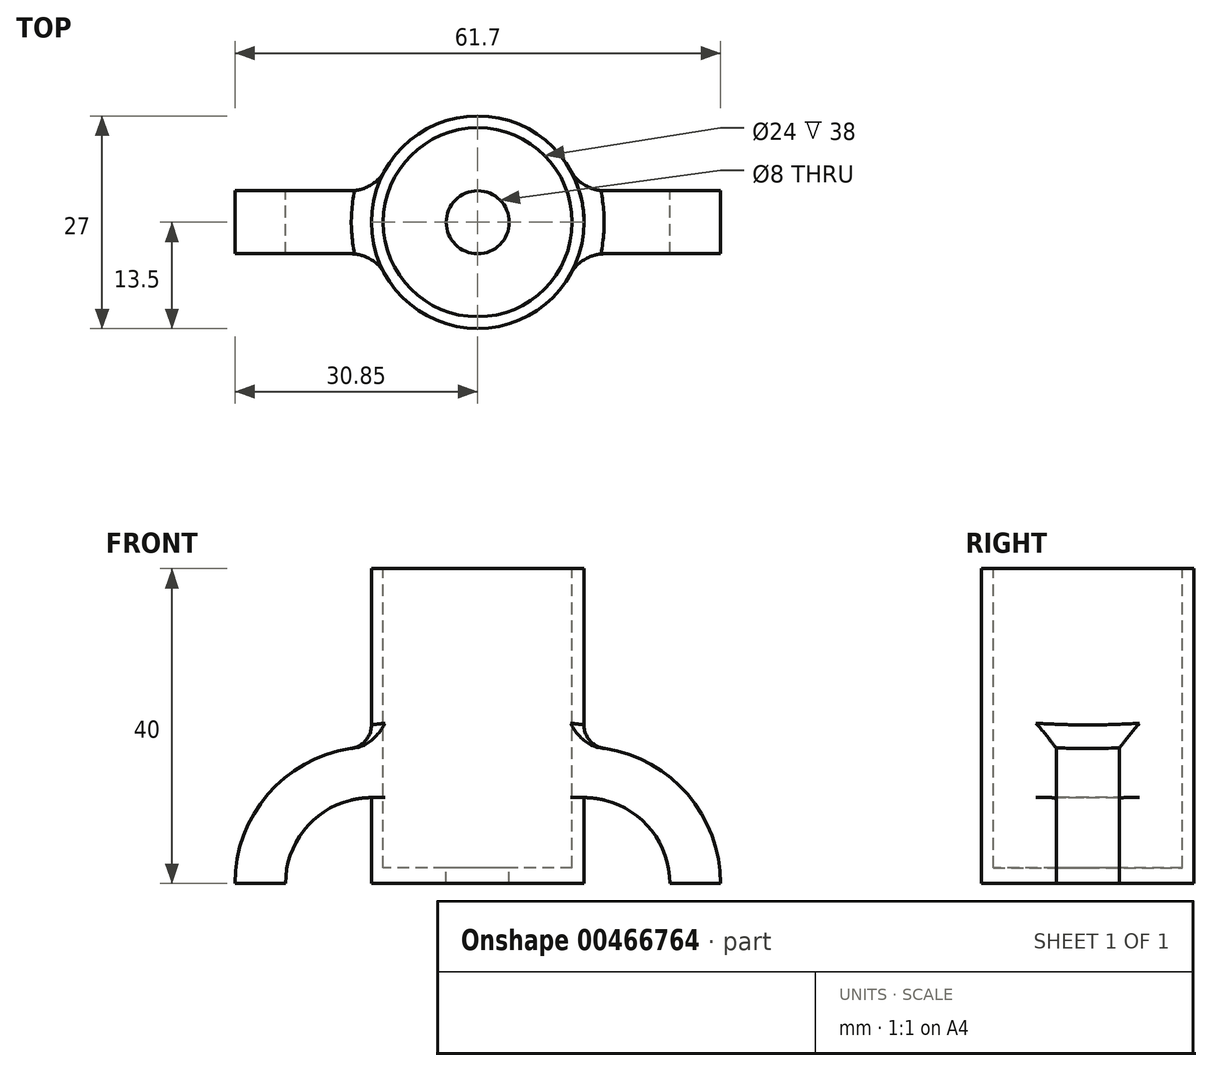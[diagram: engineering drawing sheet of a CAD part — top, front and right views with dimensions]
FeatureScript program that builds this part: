
annotation { "Feature Type Name" : "Feature", "Feature Type Description" : "" }
export const myFeature = defineFeature(function(context is Context, id is Id, definition is map)
    precondition{}
    {
        {
            var Q0;
            Q0=qCreatedBy(makeId("Top.planeOp"),FACE);
            var sketch = newSketch(context, id + "F0", { "sketchPlane" : qUnion([Q0])});
            skCircle(sketch, "E0", {"center": v(0, 0) * mm, "radius": 13.5 * mm});
            skSolve(sketch);
        }
        {
            var Q0;
            Q0=makeQuery(id+"F0.imprint","IMPRINT",FACE,{"disambiguationData":[TD([[makeQuery(id+"F0.imprint","IMPRINT",EDGE,{"derivedFrom":sQuery(id+"F0.wireOp",EDGE,"E0")}),1.0]])]});
            extrude(context, id + "F1", {"entities" : qUnion([Q0]), "depth" : 40 * mm});
        }
        {
            var Q0;
            Q0=qCreatedBy(makeId("Front.planeOp"),FACE);
            var sketch = newSketch(context, id + "F2", { "sketchPlane" : qUnion([Q0])});
            skLineSegment(sketch, "E1", {"start": v(-13.5, 0) * mm, "end": v(-13.5, 40) * mm, "construction": true});
            skLineSegment(sketch, "E2", {"start": v(13.5, 40) * mm, "end": v(13.5, 0) * mm, "construction": true});
            skArc(sketch, "E3", {"start": v(-13.5, 17.35) * mm, "mid": v(-25.77, 12.27) * mm, "end": v(-30.85, 0) * mm});
            skArc(sketch, "E4", {"start": v(-13.5, 10.91) * mm, "mid": v(-21.22, 7.72) * mm, "end": v(-24.41, 0) * mm});
            skLineSegment(sketch, "E5", {"start": v(-30.85, 0) * mm, "end": v(-24.41, 0) * mm});
            skLineSegment(sketch, "E6.bottom", {"start": v(-13.5, 17.35) * mm, "end": v(0, 17.35) * mm});
            skLineSegment(sketch, "E6.top", {"start": v(-13.5, 10.91) * mm, "end": v(0, 10.91) * mm});
            skLineSegment(sketch, "E6.left", {"start": v(-13.5, 17.35) * mm, "end": v(-13.5, 10.91) * mm});
            skLineSegment(sketch, "E6.right", {"start": v(0, 17.35) * mm, "end": v(0, 10.91) * mm});
            skArc(sketch, "E7.MirrorCS", {"start": v(13.5, 17.35) * mm, "mid": v(25.77, 12.27) * mm, "end": v(30.85, 0) * mm});
            skLineSegment(sketch, "E8.MirrorCS", {"start": v(13.5, 17.35) * mm, "end": v(0, 17.35) * mm});
            skLineSegment(sketch, "E9.MirrorCS", {"start": v(13.5, 10.91) * mm, "end": v(0, 10.91) * mm});
            skArc(sketch, "E10.MirrorCS", {"start": v(13.5, 10.91) * mm, "mid": v(21.22, 7.72) * mm, "end": v(24.41, 0) * mm});
            skLineSegment(sketch, "E11.MirrorCS", {"start": v(30.85, 0) * mm, "end": v(24.41, 0) * mm});
            skSolve(sketch);
        }
        {
            var Q0;
            Q0 = qSketchRegion(id + "F2", true);
            extrude(context, id + "F3", {"entities" : qUnion([Q0]), "operationType" : NewBodyOperationType.ADD, "endBound" : BoundingType.SYMMETRIC, "depth" : 8 * mm});
        }
        {
            var Q0;
            Q0=makeQuery(id+"F1.opExtrude","CAP_FACE",FACE,{"disambiguationData":[OSD([sQuery(id+"F0.wireOp",EDGE,"E0")])],"isStart":false});
            var sketch = newSketch(context, id + "F4", { "sketchPlane" : qUnion([Q0])});
            skCircle(sketch, "E12", {"center": v(0, 0) * mm, "radius": 12 * mm});
            skSolve(sketch);
        }
        {
            var Q0;
            Q0=makeQuery(id+"F4.imprint","IMPRINT",FACE,{"disambiguationData":[TD([[makeQuery(id+"F4.imprint","IMPRINT",EDGE,{"derivedFrom":sQuery(id+"F4.wireOp",EDGE,"E12")}),1.0]])]});
            extrude(context, id + "F5", {"entities" : qUnion([Q0]), "operationType" : NewBodyOperationType.REMOVE, "oppositeDirection" : true, "depth" : 38 * mm});
        }
        {
            var Q0;
            Q0=makeQuery(id+"F5.boolean.opBoolean","COPY",FACE,{"derivedFrom":makeQuery(id+"F5.opExtrude","CAP_FACE",FACE,{"disambiguationData":[OSD([sQuery(id+"F4.wireOp",EDGE,"E12")])],"isStart":false})});
            var sketch = newSketch(context, id + "F6", { "sketchPlane" : qUnion([Q0])});
            skCircle(sketch, "E13", {"center": v(0, 0) * mm, "radius": 4 * mm});
            skSolve(sketch);
        }
        {
            var Q0;
            Q0=makeQuery(id+"F6.imprint","IMPRINT",FACE,{"disambiguationData":[TD([[makeQuery(id+"F6.imprint","IMPRINT",EDGE,{"derivedFrom":sQuery(id+"F6.wireOp",EDGE,"E13")}),1.0]])]});
            extrude(context, id + "F7", {"entities" : qUnion([Q0]), "operationType" : NewBodyOperationType.REMOVE, "endBound" : BoundingType.UP_TO_NEXT, "oppositeDirection" : true, "depth" : 25 * mm});
        }
        {
            var Q0;
            Q0=makeQuery(id+"F3.boolean.opBoolean","INTERSECT",EDGE,{"disambiguationData":[OD(3.0)],"derivedFrom":[makeQuery(id+"F1.opExtrude","SWEPT_FACE",FACE,{"disambiguationData":[OSD([sQuery(id+"F0.wireOp",EDGE,"E0")])]}),makeQuery(id+"F3.opExtrude","SWEPT_FACE",FACE,{"disambiguationData":[OSD([sQuery(id+"F2.wireOp",EDGE,"E6.bottom"),sQuery(id+"F2.wireOp",EDGE,"E8.MirrorCS")])]})]});
            var Q1;
            Q1=makeQuery(id+"F3.boolean.opBoolean","INTERSECT",EDGE,{"disambiguationData":[OD(1.0)],"derivedFrom":[makeQuery(id+"F1.opExtrude","SWEPT_FACE",FACE,{"disambiguationData":[OSD([sQuery(id+"F0.wireOp",EDGE,"E0")])]}),makeQuery(id+"F3.opExtrude","SWEPT_FACE",FACE,{"disambiguationData":[OSD([sQuery(id+"F2.wireOp",EDGE,"E6.bottom"),sQuery(id+"F2.wireOp",EDGE,"E8.MirrorCS")])]})]});
            fillet(context, id + "F8", {"entities" : qUnion([Q0, Q1]), "radius" : 3 * mm, "tangentPropagation" : true, "allowEdgeOverflow" : false});
        }
        {
            var Q0;
            Q0=makeQuery(id+"F3.boolean.opBoolean","INTERSECT",EDGE,{"disambiguationData":[OD(1.0)],"derivedFrom":[makeQuery(id+"F1.opExtrude","SWEPT_FACE",FACE,{"disambiguationData":[OSD([sQuery(id+"F0.wireOp",EDGE,"E0")])]}),makeQuery(id+"F3.opExtrude","CAP_FACE",FACE,{"disambiguationData":[OSD([sQuery(id+"F2.wireOp",EDGE,"E3"),sQuery(id+"F2.wireOp",EDGE,"E4"),sQuery(id+"F2.wireOp",EDGE,"E5"),sQuery(id+"F2.wireOp",EDGE,"E6.bottom"),sQuery(id+"F2.wireOp",EDGE,"E6.top"),sQuery(id+"F2.wireOp",EDGE,"E7.MirrorCS"),sQuery(id+"F2.wireOp",EDGE,"E8.MirrorCS"),sQuery(id+"F2.wireOp",EDGE,"E9.MirrorCS"),sQuery(id+"F2.wireOp",EDGE,"E10.MirrorCS"),sQuery(id+"F2.wireOp",EDGE,"E11.MirrorCS")])],"isStart":true})]});
            var Q1;
            Q1=makeQuery(id+"F3.boolean.opBoolean","INTERSECT",EDGE,{"disambiguationData":[OD(1.0)],"derivedFrom":[makeQuery(id+"F1.opExtrude","SWEPT_FACE",FACE,{"disambiguationData":[OSD([sQuery(id+"F0.wireOp",EDGE,"E0")])]}),makeQuery(id+"F3.opExtrude","CAP_FACE",FACE,{"disambiguationData":[OSD([sQuery(id+"F2.wireOp",EDGE,"E3"),sQuery(id+"F2.wireOp",EDGE,"E4"),sQuery(id+"F2.wireOp",EDGE,"E5"),sQuery(id+"F2.wireOp",EDGE,"E6.bottom"),sQuery(id+"F2.wireOp",EDGE,"E6.top"),sQuery(id+"F2.wireOp",EDGE,"E7.MirrorCS"),sQuery(id+"F2.wireOp",EDGE,"E8.MirrorCS"),sQuery(id+"F2.wireOp",EDGE,"E9.MirrorCS"),sQuery(id+"F2.wireOp",EDGE,"E10.MirrorCS"),sQuery(id+"F2.wireOp",EDGE,"E11.MirrorCS")])],"isStart":false})]});
            var Q2;
            Q2=makeQuery(id+"F3.boolean.opBoolean","INTERSECT",EDGE,{"disambiguationData":[OD(0.0)],"derivedFrom":[makeQuery(id+"F1.opExtrude","SWEPT_FACE",FACE,{"disambiguationData":[OSD([sQuery(id+"F0.wireOp",EDGE,"E0")])]}),makeQuery(id+"F3.opExtrude","CAP_FACE",FACE,{"disambiguationData":[OSD([sQuery(id+"F2.wireOp",EDGE,"E3"),sQuery(id+"F2.wireOp",EDGE,"E4"),sQuery(id+"F2.wireOp",EDGE,"E5"),sQuery(id+"F2.wireOp",EDGE,"E6.bottom"),sQuery(id+"F2.wireOp",EDGE,"E6.top"),sQuery(id+"F2.wireOp",EDGE,"E7.MirrorCS"),sQuery(id+"F2.wireOp",EDGE,"E8.MirrorCS"),sQuery(id+"F2.wireOp",EDGE,"E9.MirrorCS"),sQuery(id+"F2.wireOp",EDGE,"E10.MirrorCS"),sQuery(id+"F2.wireOp",EDGE,"E11.MirrorCS")])],"isStart":false})]});
            var Q3;
            Q3=makeQuery(id+"F3.boolean.opBoolean","INTERSECT",EDGE,{"disambiguationData":[OD(0.0)],"derivedFrom":[makeQuery(id+"F1.opExtrude","SWEPT_FACE",FACE,{"disambiguationData":[OSD([sQuery(id+"F0.wireOp",EDGE,"E0")])]}),makeQuery(id+"F3.opExtrude","CAP_FACE",FACE,{"disambiguationData":[OSD([sQuery(id+"F2.wireOp",EDGE,"E3"),sQuery(id+"F2.wireOp",EDGE,"E4"),sQuery(id+"F2.wireOp",EDGE,"E5"),sQuery(id+"F2.wireOp",EDGE,"E6.bottom"),sQuery(id+"F2.wireOp",EDGE,"E6.top"),sQuery(id+"F2.wireOp",EDGE,"E7.MirrorCS"),sQuery(id+"F2.wireOp",EDGE,"E8.MirrorCS"),sQuery(id+"F2.wireOp",EDGE,"E9.MirrorCS"),sQuery(id+"F2.wireOp",EDGE,"E10.MirrorCS"),sQuery(id+"F2.wireOp",EDGE,"E11.MirrorCS")])],"isStart":true})]});
            fillet(context, id + "F9", {"entities" : qUnion([Q0, Q1, Q2, Q3]), "radius" : 5 * mm, "tangentPropagation" : true, "allowEdgeOverflow" : false});
        }
    });
